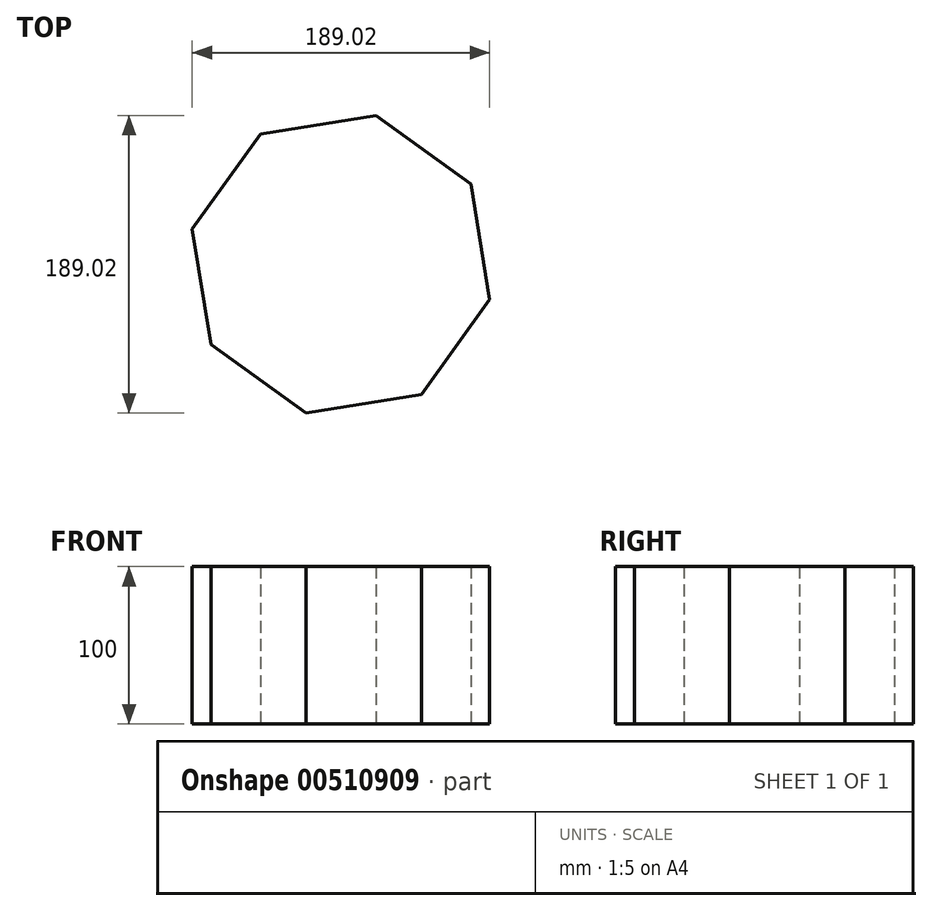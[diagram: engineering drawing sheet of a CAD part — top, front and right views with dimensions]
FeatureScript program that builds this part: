
annotation { "Feature Type Name" : "Feature", "Feature Type Description" : "" }
export const myFeature = defineFeature(function(context is Context, id is Id, definition is map)
    precondition{}
    {
        {
            var Q0;
            Q0=qCreatedBy(makeId("Top.planeOp"),FACE);
            var sketch = newSketch(context, id + "F0", { "sketchPlane" : qUnion([Q0])});
            skCircle(sketch, "E0.cCircle", {"center": v(0, 0) * mm, "radius": 97.1 * mm, "construction": true});
            skLineSegment(sketch, "E0.0", {"start": v(51.07, -82.59) * mm, "end": v(-22.3, -94.5) * mm});
            skLineSegment(sketch, "E0.1", {"start": v(-22.3, -94.5) * mm, "end": v(-82.59, -51.07) * mm});
            skLineSegment(sketch, "E0.2", {"start": v(-82.59, -51.07) * mm, "end": v(-94.5, 22.3) * mm});
            skLineSegment(sketch, "E0.3", {"start": v(-94.5, 22.3) * mm, "end": v(-51.07, 82.59) * mm});
            skLineSegment(sketch, "E0.4", {"start": v(-51.07, 82.59) * mm, "end": v(22.3, 94.5) * mm});
            skLineSegment(sketch, "E0.5", {"start": v(22.3, 94.5) * mm, "end": v(82.59, 51.07) * mm});
            skLineSegment(sketch, "E0.6", {"start": v(82.59, 51.07) * mm, "end": v(94.5, -22.3) * mm});
            skLineSegment(sketch, "E0.7", {"start": v(94.5, -22.3) * mm, "end": v(51.07, -82.59) * mm});
            skSolve(sketch);
        }
        {
            var Q0;
            Q0 = qSketchRegion(id + "F0", true);
            extrude(context, id + "F1", {"entities" : qUnion([Q0]), "depth" : 100 * mm});
        }
    });
